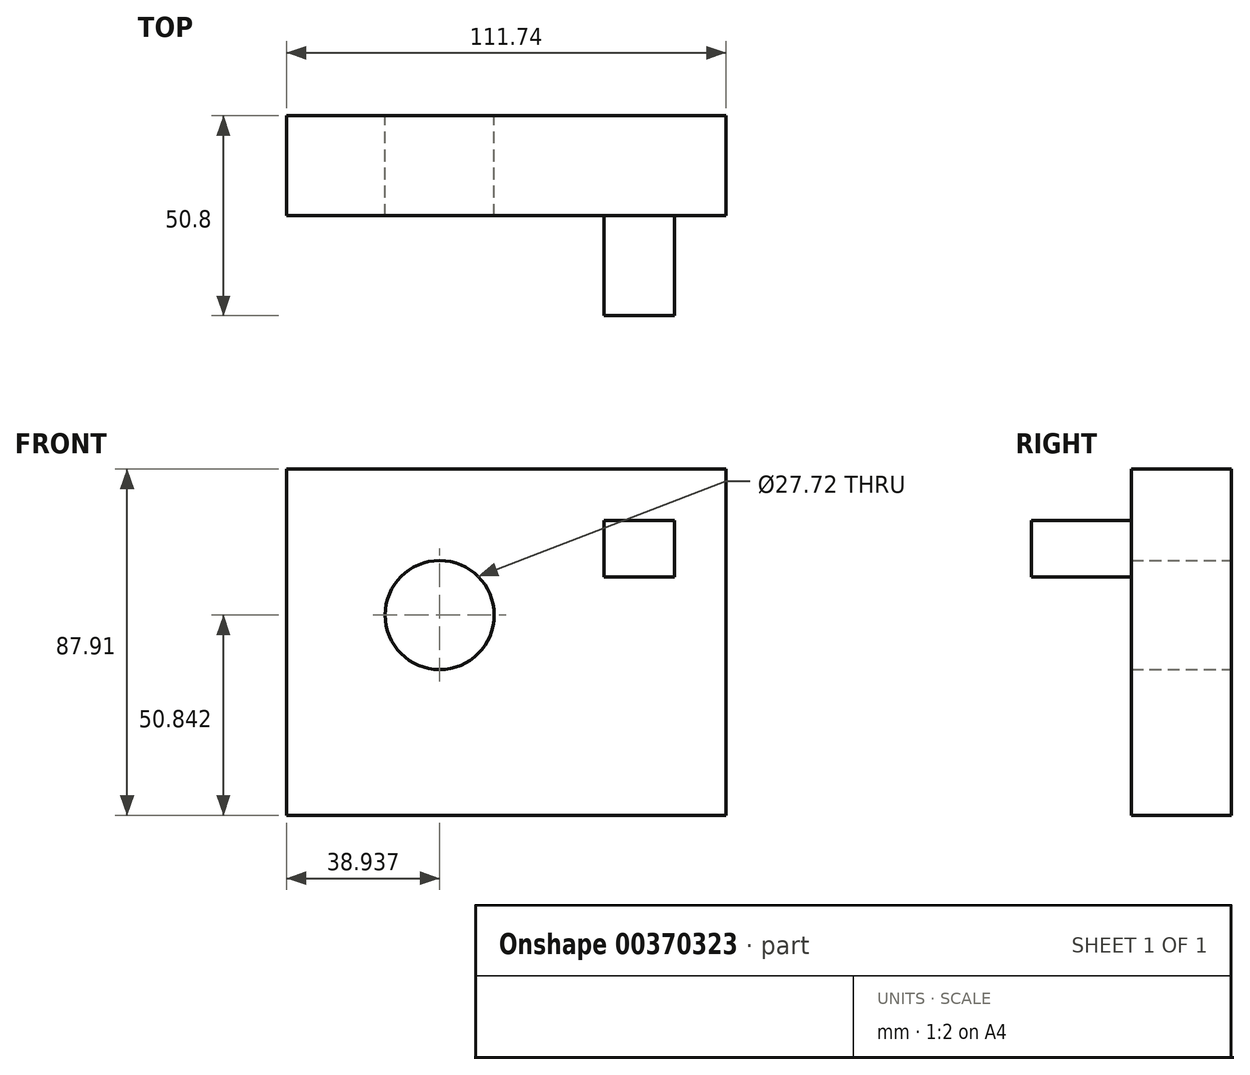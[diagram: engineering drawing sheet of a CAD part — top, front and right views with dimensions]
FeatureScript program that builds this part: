
annotation { "Feature Type Name" : "Feature", "Feature Type Description" : "" }
export const myFeature = defineFeature(function(context is Context, id is Id, definition is map)
    precondition{}
    {
        {
            var Q0;
            Q0=qCreatedBy(makeId("Front.planeOp"),FACE);
            var sketch = newSketch(context, id + "F0", { "sketchPlane" : qUnion([Q0])});
            skLineSegment(sketch, "E0.bottom", {"start": v(-59.27, 51.94) * mm, "end": v(52.47, 51.94) * mm});
            skLineSegment(sketch, "E0.top", {"start": v(-59.27, -35.97) * mm, "end": v(52.47, -35.97) * mm});
            skLineSegment(sketch, "E0.left", {"start": v(-59.27, 51.94) * mm, "end": v(-59.27, -35.97) * mm});
            skLineSegment(sketch, "E0.right", {"start": v(52.47, 51.94) * mm, "end": v(52.47, -35.97) * mm});
            skCircle(sketch, "E1", {"center": v(-20.33, 14.87) * mm, "radius": 13.86 * mm});
            skSolve(sketch);
        }
        {
            var Q0;
            Q0=makeQuery(id+"F0.imprint","IMPRINT",FACE,{"disambiguationData":[TD([[makeQuery(id+"F0.imprint","IMPRINT",EDGE,{"derivedFrom":sQuery(id+"F0.wireOp",EDGE,"E0.bottom")}),-1.0]])]});
            extrude(context, id + "F1", {"entities" : qUnion([Q0]), "depth" : 25.4 * mm});
        }
        {
            var Q0;
            Q0=makeQuery(id+"F1.opExtrude","CAP_FACE",FACE,{"disambiguationData":[OSD([sQuery(id+"F0.wireOp",EDGE,"E0.bottom"),sQuery(id+"F0.wireOp",EDGE,"E0.top"),sQuery(id+"F0.wireOp",EDGE,"E0.left"),sQuery(id+"F0.wireOp",EDGE,"E0.right"),sQuery(id+"F0.wireOp",EDGE,"E1")])],"isStart":false});
            var sketch = newSketch(context, id + "F2", { "sketchPlane" : qUnion([Q0])});
            skLineSegment(sketch, "E2.bottom", {"start": v(21.47, 38.93) * mm, "end": v(39.38, 38.93) * mm});
            skLineSegment(sketch, "E2.top", {"start": v(21.47, 24.5) * mm, "end": v(39.38, 24.5) * mm});
            skLineSegment(sketch, "E2.left", {"start": v(21.47, 38.93) * mm, "end": v(21.47, 24.5) * mm});
            skLineSegment(sketch, "E2.right", {"start": v(39.38, 38.93) * mm, "end": v(39.38, 24.5) * mm});
            skSolve(sketch);
        }
        {
            var Q0;
            Q0=makeQuery(id+"F2.imprint","IMPRINT",FACE,{"disambiguationData":[TD([[makeQuery(id+"F2.imprint","IMPRINT",EDGE,{"derivedFrom":sQuery(id+"F2.wireOp",EDGE,"E2.bottom")}),-1.0]])]});
            extrude(context, id + "F3", {"entities" : qUnion([Q0]), "operationType" : NewBodyOperationType.ADD, "depth" : 25.4 * mm});
        }
    });
